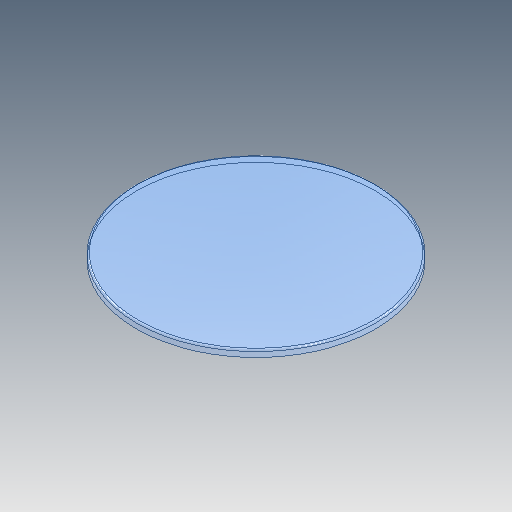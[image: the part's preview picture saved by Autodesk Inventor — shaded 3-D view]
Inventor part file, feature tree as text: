
AUTODESK INVENTOR PART (.ipt)
format: ipt  version: 2020.3 (Build 243373000, 373)  size: 103,424 bytes
history: native  units: mm
features: extrude x1, fillet x1, sketch x1
ambient origin geometry x8: Origin, YZ Plane, XZ Plane, XY Plane, X Axis, Y Axis, Z Axis, Center Point
bodies: Solid1 (feature_tree)
feature tree (3):
  extrude  "Extrusion1"  Depth=2.0mm TaperAngle=0.0deg
  fillet  "Fillet1"  Radius=0.5mm
  sketch  "Sketch1"  dims[d0=70.0mm d1=2.0mm d2=0.0mm d3=0.5mm]
